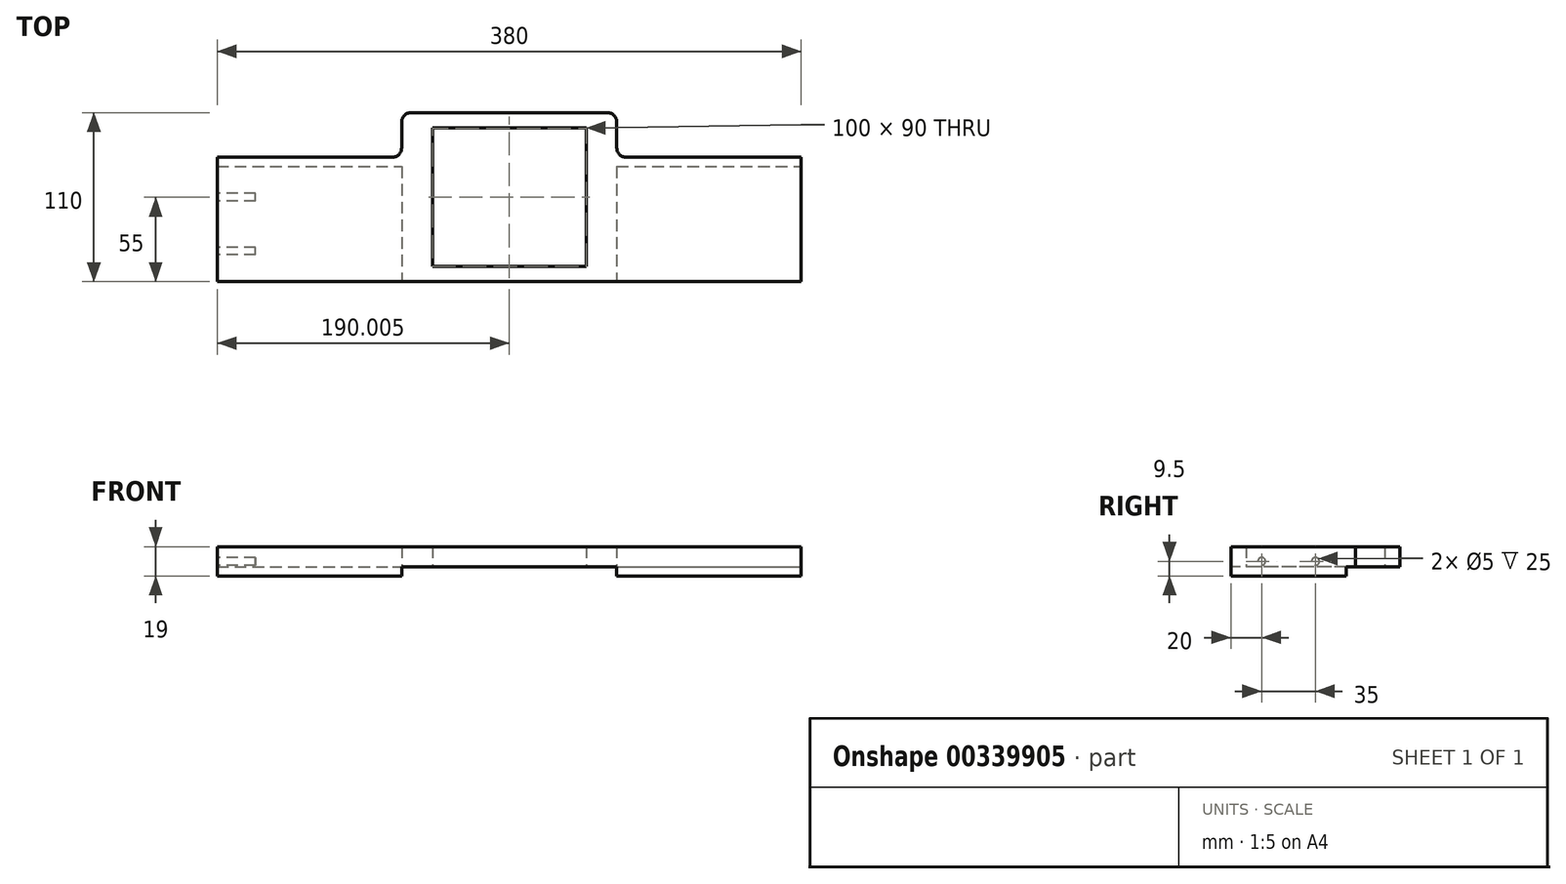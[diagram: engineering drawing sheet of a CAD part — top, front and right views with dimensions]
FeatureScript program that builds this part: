
annotation { "Feature Type Name" : "Feature", "Feature Type Description" : "" }
export const myFeature = defineFeature(function(context is Context, id is Id, definition is map)
    precondition{}
    {
        {
            var Q0;
            Q0=qCreatedBy(makeId("Top.planeOp"),FACE);
            var sketch = newSketch(context, id + "F0", { "sketchPlane" : qUnion([Q0])});
            skLineSegment(sketch, "E0.bottom", {"start": v(-30.79, 58.62) * mm, "end": v(349.21, 58.62) * mm});
            skLineSegment(sketch, "E0.top", {"start": v(-30.79, -22.38) * mm, "end": v(349.21, -22.38) * mm});
            skLineSegment(sketch, "E0.left", {"start": v(-30.79, 58.62) * mm, "end": v(-30.79, -22.38) * mm});
            skLineSegment(sketch, "E0.right", {"start": v(349.21, 58.62) * mm, "end": v(349.21, -22.38) * mm});
            skLineSegment(sketch, "E1", {"start": v(159.21, -22.38) * mm, "end": v(159.21, 87.62) * mm});
            skLineSegment(sketch, "E2", {"start": v(159.21, 87.62) * mm, "end": v(89.21, 87.62) * mm});
            skLineSegment(sketch, "E3", {"start": v(89.21, 87.62) * mm, "end": v(89.21, 58.62) * mm});
            skLineSegment(sketch, "E4.MirrorCS", {"start": v(349.21, -22.38) * mm, "end": v(-30.79, -22.38) * mm});
            skLineSegment(sketch, "E5.MirrorCS", {"start": v(229.21, 87.62) * mm, "end": v(229.21, 58.62) * mm});
            skLineSegment(sketch, "E6.MirrorCS", {"start": v(159.21, 87.62) * mm, "end": v(229.21, 87.62) * mm});
            skLineSegment(sketch, "E7.MirrorCS", {"start": v(349.21, 58.62) * mm, "end": v(-30.79, 58.62) * mm});
            skLineSegment(sketch, "E8", {"start": v(-30.79, 52.62) * mm, "end": v(95.21, 52.62) * mm});
            skLineSegment(sketch, "E9", {"start": v(229.21, 52.62) * mm, "end": v(349.21, 52.62) * mm});
            skLineSegment(sketch, "E10", {"start": v(89.21, 58.62) * mm, "end": v(89.21, 52.62) * mm});
            skLineSegment(sketch, "E11", {"start": v(229.21, 58.62) * mm, "end": v(229.21, 52.62) * mm});
            skLineSegment(sketch, "E12", {"start": v(229.21, 81.62) * mm, "end": v(89.21, 81.62) * mm});
            skLineSegment(sketch, "E13", {"start": v(229.21, 52.62) * mm, "end": v(223.21, 52.62) * mm});
            skLineSegment(sketch, "E14", {"start": v(223.21, 52.62) * mm, "end": v(223.21, 81.62) * mm});
            skLineSegment(sketch, "E15", {"start": v(95.21, 52.62) * mm, "end": v(95.21, 81.62) * mm});
            skLineSegment(sketch, "E16.bottom", {"start": v(109.21, 77.62) * mm, "end": v(209.21, 77.62) * mm});
            skLineSegment(sketch, "E16.top", {"start": v(109.21, -12.38) * mm, "end": v(209.21, -12.38) * mm});
            skLineSegment(sketch, "E16.left", {"start": v(109.21, 77.62) * mm, "end": v(109.21, -12.38) * mm});
            skLineSegment(sketch, "E16.right", {"start": v(209.21, 77.62) * mm, "end": v(209.21, -12.38) * mm});
            skLineSegment(sketch, "E17", {"start": v(229.21, 52.62) * mm, "end": v(229.21, -22.38) * mm});
            skLineSegment(sketch, "E18", {"start": v(89.21, 52.62) * mm, "end": v(89.21, -22.38) * mm});
            skSolve(sketch);
        }
        {
            var Q0;
            Q0 = qSketchRegion(id + "F0", true);
            var Q1;
            {var subQ5=sQuery(id+"F0.wireOp",EDGE,"E1");var subQ9=sQuery(id+"F0.wireOp",EDGE,"E16.bottom");var subQ11=makeQuery(id+"F0.imprint","INTERSECT",VERTEX,{"derivedFrom":[subQ5,subQ9]});Q1=makeQuery(id+"F0.imprint","IMPRINT",FACE,{"disambiguationData":[TD([[makeQuery(id+"F0.imprint","IMPRINT",EDGE,{"disambiguationData":[TD([[subQ11,-1.0]])],"derivedFrom":subQ5}),1.0]])]});}
            var Q2;
            {var subQ5=sQuery(id+"F0.wireOp",EDGE,"E1");var subQ9=sQuery(id+"F0.wireOp",EDGE,"E16.bottom");var subQ11=makeQuery(id+"F0.imprint","INTERSECT",VERTEX,{"derivedFrom":[subQ5,subQ9]});Q2=makeQuery(id+"F0.imprint","IMPRINT",FACE,{"disambiguationData":[TD([[makeQuery(id+"F0.imprint","IMPRINT",EDGE,{"disambiguationData":[TD([[subQ11,-1.0]])],"derivedFrom":subQ5}),-1.0]])]});}
            extrude(context, id + "F1", {"entities" : qUnion([Q0, Q1, Q2]), "depth" : 19 * mm, "offsetDistance" : 25 * mm});
        }
        {
            var Q0;
            {var subQ3=sQuery(id+"F0.wireOp",EDGE,"E8");Q0=makeQuery(id+"F0.imprint","IMPRINT",FACE,{"disambiguationData":[TD([[makeQuery(id+"F0.imprint","IMPRINT",EDGE,{"derivedFrom":subQ3}),1.0]])]});}
            var Q1;
            {var subQ5=sQuery(id+"F0.wireOp",EDGE,"E11");Q1=makeQuery(id+"F0.imprint","IMPRINT",FACE,{"disambiguationData":[TD([[makeQuery(id+"F0.imprint","IMPRINT",EDGE,{"derivedFrom":subQ5}),1.0]])]});}
            var Q2;
            {var subQ1=sQuery(id+"F0.wireOp",EDGE,"E3");var subQ3=sQuery(id+"F0.wireOp",EDGE,"E12");var subQ4=makeQuery(id+"F0.imprint","INTERSECT",VERTEX,{"derivedFrom":[subQ1,subQ3]});Q2=makeQuery(id+"F0.imprint","IMPRINT",FACE,{"disambiguationData":[TD([[makeQuery(id+"F0.imprint","IMPRINT",EDGE,{"disambiguationData":[TD([[subQ4,1.0]])],"derivedFrom":subQ3}),1.0]])]});}
            var Q3;
            {var subQ5=sQuery(id+"F0.wireOp",EDGE,"E2");Q3=makeQuery(id+"F0.imprint","IMPRINT",FACE,{"disambiguationData":[TD([[makeQuery(id+"F0.imprint","IMPRINT",EDGE,{"derivedFrom":subQ5}),1.0]])]});}
            var Q4;
            {var subQ4=sQuery(id+"F0.wireOp",EDGE,"E6.MirrorCS");Q4=makeQuery(id+"F0.imprint","IMPRINT",FACE,{"disambiguationData":[TD([[makeQuery(id+"F0.imprint","IMPRINT",EDGE,{"derivedFrom":subQ4}),-1.0]])]});}
            var Q5;
            {var subQ1=sQuery(id+"F0.wireOp",EDGE,"E5.MirrorCS");var subQ3=sQuery(id+"F0.wireOp",EDGE,"E12");var subQ4=makeQuery(id+"F0.imprint","INTERSECT",VERTEX,{"derivedFrom":[subQ1,subQ3]});Q5=makeQuery(id+"F0.imprint","IMPRINT",FACE,{"disambiguationData":[TD([[makeQuery(id+"F0.imprint","IMPRINT",EDGE,{"disambiguationData":[TD([[subQ4,-1.0]])],"derivedFrom":subQ3}),1.0]])]});}
            var Q6;
            {var subQ1=sQuery(id+"F0.wireOp",EDGE,"E11");Q6=makeQuery(id+"F0.imprint","IMPRINT",FACE,{"disambiguationData":[TD([[makeQuery(id+"F0.imprint","IMPRINT",EDGE,{"derivedFrom":subQ1}),-1.0]])]});}
            var Q7;
            {var subQ0=sQuery(id+"F0.wireOp",EDGE,"E17");Q7=makeQuery(id+"F0.imprint","IMPRINT",FACE,{"disambiguationData":[TD([[makeQuery(id+"F0.imprint","IMPRINT",EDGE,{"derivedFrom":subQ0}),-1.0]])]});}
            var Q8;
            {var subQ3=sQuery(id+"F0.wireOp",EDGE,"E18");Q8=makeQuery(id+"F0.imprint","IMPRINT",FACE,{"disambiguationData":[TD([[makeQuery(id+"F0.imprint","IMPRINT",EDGE,{"derivedFrom":subQ3}),1.0]])]});}
            var Q9;
            {var subQ5=sQuery(id+"F0.wireOp",EDGE,"E1");var subQ9=sQuery(id+"F0.wireOp",EDGE,"E16.bottom");var subQ11=makeQuery(id+"F0.imprint","INTERSECT",VERTEX,{"derivedFrom":[subQ5,subQ9]});Q9=makeQuery(id+"F0.imprint","IMPRINT",FACE,{"disambiguationData":[TD([[makeQuery(id+"F0.imprint","IMPRINT",EDGE,{"disambiguationData":[TD([[subQ11,-1.0]])],"derivedFrom":subQ5}),-1.0]])]});}
            var Q10;
            {var subQ5=sQuery(id+"F0.wireOp",EDGE,"E1");var subQ9=sQuery(id+"F0.wireOp",EDGE,"E16.bottom");var subQ11=makeQuery(id+"F0.imprint","INTERSECT",VERTEX,{"derivedFrom":[subQ5,subQ9]});Q10=makeQuery(id+"F0.imprint","IMPRINT",FACE,{"disambiguationData":[TD([[makeQuery(id+"F0.imprint","IMPRINT",EDGE,{"disambiguationData":[TD([[subQ11,-1.0]])],"derivedFrom":subQ5}),1.0]])]});}
            extrude(context, id + "F2", {"entities" : qUnion([Q0, Q1, Q2, Q3, Q4, Q5, Q6, Q7, Q8, Q9, Q10]), "operationType" : NewBodyOperationType.REMOVE, "depth" : 6 * mm, "offsetDistance" : 25 * mm});
        }
        {
            var Q0;
            Q0=makeQuery(id+"F1.opExtrude","SWEPT_EDGE",EDGE,{"disambiguationData":[OSD([sQuery(id+"F0.wireOp",EDGE,"E5.MirrorCS"),sQuery(id+"F0.wireOp",EDGE,"E7.MirrorCS"),sQuery(id+"F0.wireOp",EDGE,"E11")])]});
            var Q1;
            Q1=makeQuery(id+"F1.opExtrude","SWEPT_EDGE",EDGE,{"disambiguationData":[OSD([sQuery(id+"F0.wireOp",EDGE,"E5.MirrorCS"),sQuery(id+"F0.wireOp",EDGE,"E6.MirrorCS")])]});
            var Q2;
            Q2=makeQuery(id+"F1.opExtrude","SWEPT_EDGE",EDGE,{"disambiguationData":[OSD([sQuery(id+"F0.wireOp",EDGE,"E2"),sQuery(id+"F0.wireOp",EDGE,"E3")])]});
            var Q3;
            Q3=makeQuery(id+"F1.opExtrude","SWEPT_EDGE",EDGE,{"disambiguationData":[OSD([sQuery(id+"F0.wireOp",EDGE,"E3"),sQuery(id+"F0.wireOp",EDGE,"E7.MirrorCS"),sQuery(id+"F0.wireOp",EDGE,"E10")])]});
            var Q4;
            Q4=makeQuery(id+"F2.boolean.opBoolean","COPY",EDGE,{"derivedFrom":makeQuery(id+"F2.opExtrude","SWEPT_EDGE",EDGE,{"disambiguationData":[OSD([sQuery(id+"F0.wireOp",EDGE,"E12"),sQuery(id+"F0.wireOp",EDGE,"E14")])]})});
            var Q5;
            Q5=makeQuery(id+"F2.boolean.opBoolean","COPY",EDGE,{"derivedFrom":makeQuery(id+"F2.opExtrude","SWEPT_EDGE",EDGE,{"disambiguationData":[OSD([sQuery(id+"F0.wireOp",EDGE,"E12"),sQuery(id+"F0.wireOp",EDGE,"E15")])]})});
            fillet(context, id + "F3", {"entities" : qUnion([Q0, Q1, Q2, Q3, Q4, Q5]), "radius" : 6 * mm, "tangentPropagation" : true, "allowEdgeOverflow" : false});
        }
        {
            var Q0;
            Q0=makeQuery(id+"F1.opExtrude","SWEPT_FACE",FACE,{"disambiguationData":[OSD([sQuery(id+"F0.wireOp",EDGE,"E0.left")])]});
            var sketch = newSketch(context, id + "F4", { "sketchPlane" : qUnion([Q0])});
            skCircle(sketch, "E19", {"center": v(-32.62, 9.5) * mm, "radius": 2.5 * mm});
            skCircle(sketch, "E20", {"center": v(2.38, 9.5) * mm, "radius": 2.5 * mm});
            skSolve(sketch);
        }
        {
            var Q0;
            Q0 = qSketchRegion(id + "F4", true);
            extrude(context, id + "F5", {"entities" : qUnion([Q0]), "operationType" : NewBodyOperationType.REMOVE, "oppositeDirection" : true, "depth" : 25 * mm, "offsetDistance" : 25 * mm});
        }
    });
